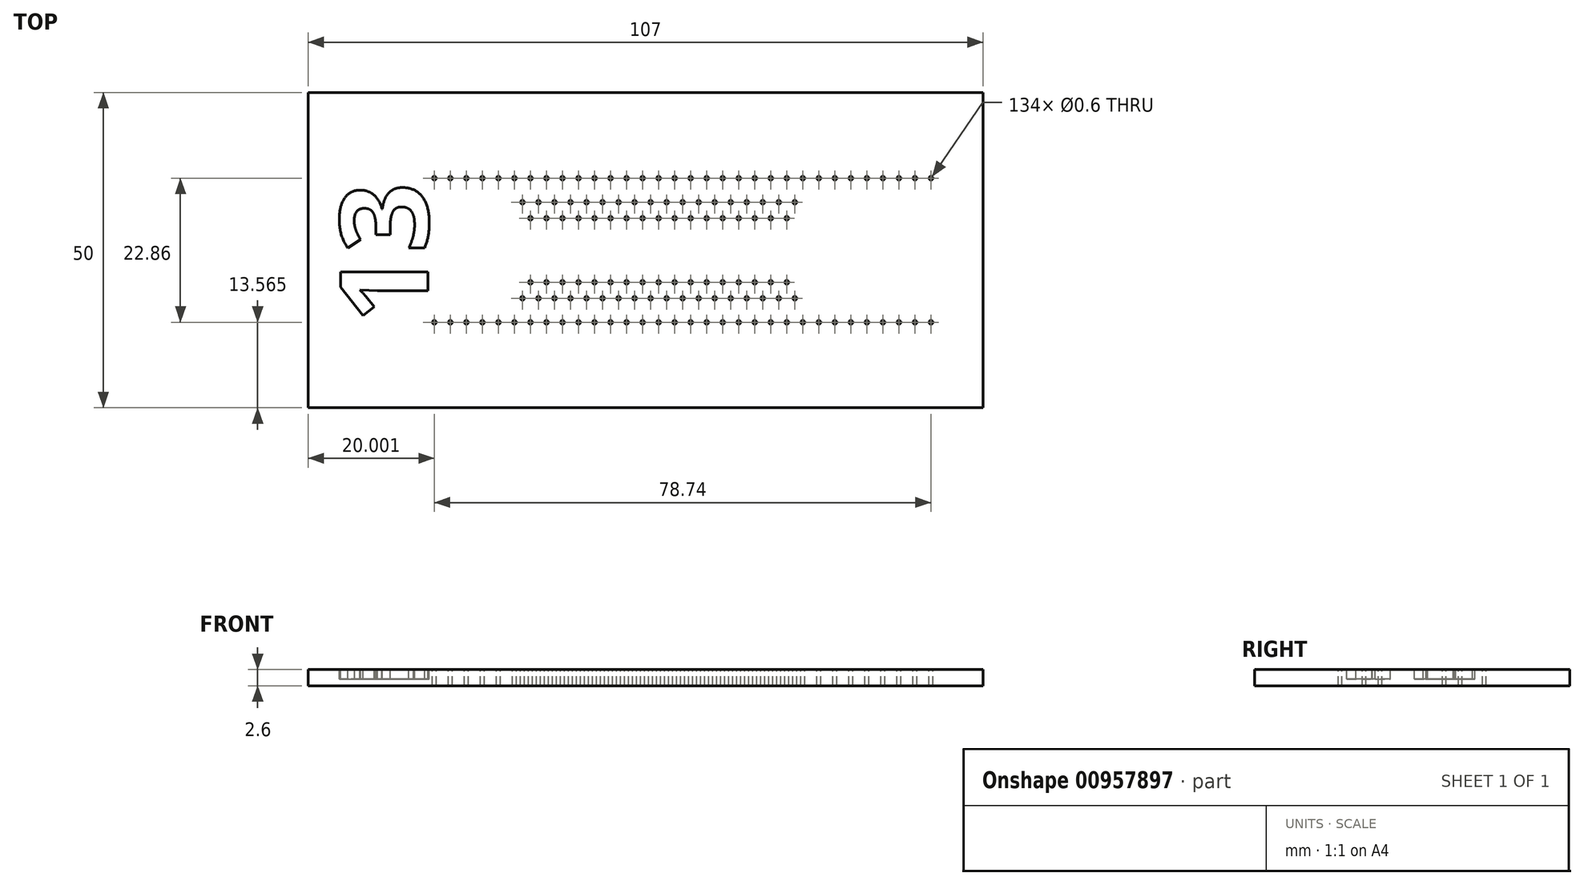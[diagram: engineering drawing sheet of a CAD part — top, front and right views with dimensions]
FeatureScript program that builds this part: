
annotation { "Feature Type Name" : "Feature", "Feature Type Description" : "" }
export const myFeature = defineFeature(function(context is Context, id is Id, definition is map)
    precondition{}
    {
        {
            var Q0;
            Q0=qCreatedBy(makeId("Top.planeOp"),FACE);
            var sketch = newSketch(context, id + "F0", { "sketchPlane" : qUnion([Q0])});
            skLineSegment(sketch, "E0.bottom", {"start": v(-43.16, 28.34) * mm, "end": v(63.84, 28.34) * mm});
            skLineSegment(sketch, "E0.top", {"start": v(-43.16, -21.66) * mm, "end": v(63.84, -21.66) * mm});
            skLineSegment(sketch, "E0.left", {"start": v(-43.16, 28.34) * mm, "end": v(-43.16, -21.66) * mm});
            skLineSegment(sketch, "E0.right", {"start": v(63.84, 28.34) * mm, "end": v(63.84, -21.66) * mm});
            skSolve(sketch);
        }
        {
            var Q0;
            Q0=makeQuery(id+"F0.imprint","IMPRINT",FACE,{"disambiguationData":[TD([[makeQuery(id+"F0.imprint","IMPRINT",EDGE,{"derivedFrom":sQuery(id+"F0.wireOp",EDGE,"E0.bottom")}),-1.0]])]});
            extrude(context, id + "F1", {"entities" : qUnion([Q0]), "depth" : 2.6 * mm, "offsetDistance" : 25 * mm});
        }
        {
            var Q0;
            Q0=makeQuery(id+"F1.opExtrude","CAP_FACE",FACE,{"disambiguationData":[OSD([sQuery(id+"F0.wireOp",EDGE,"E0.bottom"),sQuery(id+"F0.wireOp",EDGE,"E0.top"),sQuery(id+"F0.wireOp",EDGE,"E0.left"),sQuery(id+"F0.wireOp",EDGE,"E0.right")])],"isStart":false});
            var sketch = newSketch(context, id + "F2", { "sketchPlane" : qUnion([Q0])});
            skText(sketch, "E1", { "text": "13", "fontName": "OpenSans-Bold.ttf"});
            const initialGuessF2  = {"E1": [-0.02416, -0.00817, 0, 1, 0.014]};
            skSetInitialGuess(sketch, initialGuessF2);
            skSolve(sketch);
        }
        {
            var Q0;
            Q0=qSketchRegion(id+"F2",true);
            extrude(context, id + "F3", {"entities" : qUnion([Q0]), "operationType" : NewBodyOperationType.REMOVE, "oppositeDirection" : true, "depth" : 1.5 * mm, "offsetDistance" : 25 * mm});
        }
        {
            var Q0;
            {var subQ0=sQuery(id+"F0.wireOp",EDGE,"E0.left");var subQ1=sQuery(id+"F0.wireOp",EDGE,"E0.bottom");var subQ2=sQuery(id+"F0.wireOp",EDGE,"E0.right");var subQ3=sQuery(id+"F0.wireOp",EDGE,"E0.top");Q0=makeQuery(id+"F3.boolean.opBoolean","SPLIT",FACE,{"disambiguationData":[TD([makeQuery(id+"F1.opExtrude","SWEPT_FACE",FACE,{"disambiguationData":[OSD([subQ1])]})])],"derivedFrom":makeQuery(id+"F1.opExtrude","CAP_FACE",FACE,{"disambiguationData":[OSD([subQ1,subQ3,subQ0,subQ2])],"isStart":false})});}
            var sketch = newSketch(context, id + "F4", { "sketchPlane" : qUnion([Q0])});
            skCircle(sketch, "E2", {"center": v(-23.16, 14.77) * mm, "radius": 0.3 * mm});
            skCircle(sketch, "E3", {"center": v(-20.62, 14.77) * mm, "radius": 0.3 * mm});
            skCircle(sketch, "E4", {"center": v(-18.08, 14.77) * mm, "radius": 0.3 * mm});
            skCircle(sketch, "E5", {"center": v(-15.54, 14.77) * mm, "radius": 0.3 * mm});
            skCircle(sketch, "E6", {"center": v(-13, 14.77) * mm, "radius": 0.3 * mm});
            skCircle(sketch, "E7", {"center": v(-10.46, 14.77) * mm, "radius": 0.3 * mm});
            skCircle(sketch, "E8", {"center": v(-7.92, 14.77) * mm, "radius": 0.3 * mm});
            skCircle(sketch, "E9", {"center": v(-5.38, 14.77) * mm, "radius": 0.3 * mm});
            skCircle(sketch, "E10", {"center": v(-2.84, 14.77) * mm, "radius": 0.3 * mm});
            skCircle(sketch, "E11", {"center": v(-0.3, 14.77) * mm, "radius": 0.3 * mm});
            skCircle(sketch, "E12", {"center": v(2.24, 14.77) * mm, "radius": 0.3 * mm});
            skCircle(sketch, "E13", {"center": v(4.78, 14.77) * mm, "radius": 0.3 * mm});
            skCircle(sketch, "E14", {"center": v(7.32, 14.77) * mm, "radius": 0.3 * mm});
            skCircle(sketch, "E15", {"center": v(9.86, 14.77) * mm, "radius": 0.3 * mm});
            skCircle(sketch, "E16", {"center": v(12.4, 14.77) * mm, "radius": 0.3 * mm});
            skCircle(sketch, "E17", {"center": v(14.94, 14.77) * mm, "radius": 0.3 * mm});
            skCircle(sketch, "E18", {"center": v(17.48, 14.77) * mm, "radius": 0.3 * mm});
            skCircle(sketch, "E19", {"center": v(20.02, 14.77) * mm, "radius": 0.3 * mm});
            skCircle(sketch, "E20", {"center": v(22.56, 14.77) * mm, "radius": 0.3 * mm});
            skCircle(sketch, "E21", {"center": v(25.1, 14.77) * mm, "radius": 0.3 * mm});
            skCircle(sketch, "E22", {"center": v(27.64, 14.77) * mm, "radius": 0.3 * mm});
            skCircle(sketch, "E23", {"center": v(30.18, 14.77) * mm, "radius": 0.3 * mm});
            skCircle(sketch, "E24", {"center": v(32.72, 14.77) * mm, "radius": 0.3 * mm});
            skCircle(sketch, "E25", {"center": v(35.26, 14.77) * mm, "radius": 0.3 * mm});
            skCircle(sketch, "E26", {"center": v(37.8, 14.77) * mm, "radius": 0.3 * mm});
            skCircle(sketch, "E27", {"center": v(40.34, 14.77) * mm, "radius": 0.3 * mm});
            skCircle(sketch, "E28", {"center": v(42.88, 14.77) * mm, "radius": 0.3 * mm});
            skCircle(sketch, "E29", {"center": v(45.42, 14.77) * mm, "radius": 0.3 * mm});
            skCircle(sketch, "E30", {"center": v(47.96, 14.77) * mm, "radius": 0.3 * mm});
            skCircle(sketch, "E31", {"center": v(50.5, 14.77) * mm, "radius": 0.3 * mm});
            skCircle(sketch, "E32", {"center": v(53.04, 14.77) * mm, "radius": 0.3 * mm});
            skCircle(sketch, "E33", {"center": v(55.58, 14.77) * mm, "radius": 0.3 * mm});
            skCircle(sketch, "E34", {"center": v(-23.16, -8.1) * mm, "radius": 0.3 * mm});
            skCircle(sketch, "E35", {"center": v(-20.62, -8.1) * mm, "radius": 0.3 * mm});
            skCircle(sketch, "E36", {"center": v(-18.08, -8.1) * mm, "radius": 0.3 * mm});
            skCircle(sketch, "E37", {"center": v(-15.54, -8.1) * mm, "radius": 0.3 * mm});
            skCircle(sketch, "E38", {"center": v(-13, -8.1) * mm, "radius": 0.3 * mm});
            skCircle(sketch, "E39", {"center": v(-10.46, -8.1) * mm, "radius": 0.3 * mm});
            skCircle(sketch, "E40", {"center": v(-7.92, -8.1) * mm, "radius": 0.3 * mm});
            skCircle(sketch, "E41", {"center": v(-5.38, -8.1) * mm, "radius": 0.3 * mm});
            skCircle(sketch, "E42", {"center": v(-2.84, -8.1) * mm, "radius": 0.3 * mm});
            skCircle(sketch, "E43", {"center": v(-0.3, -8.1) * mm, "radius": 0.3 * mm});
            skCircle(sketch, "E44", {"center": v(2.24, -8.1) * mm, "radius": 0.3 * mm});
            skCircle(sketch, "E45", {"center": v(4.78, -8.1) * mm, "radius": 0.3 * mm});
            skCircle(sketch, "E46", {"center": v(7.32, -8.1) * mm, "radius": 0.3 * mm});
            skCircle(sketch, "E47", {"center": v(9.86, -8.1) * mm, "radius": 0.3 * mm});
            skCircle(sketch, "E48", {"center": v(12.4, -8.1) * mm, "radius": 0.3 * mm});
            skCircle(sketch, "E49", {"center": v(14.94, -8.1) * mm, "radius": 0.3 * mm});
            skCircle(sketch, "E50", {"center": v(17.48, -8.1) * mm, "radius": 0.3 * mm});
            skCircle(sketch, "E51", {"center": v(20.02, -8.1) * mm, "radius": 0.3 * mm});
            skCircle(sketch, "E52", {"center": v(22.56, -8.1) * mm, "radius": 0.3 * mm});
            skCircle(sketch, "E53", {"center": v(25.1, -8.1) * mm, "radius": 0.3 * mm});
            skCircle(sketch, "E54", {"center": v(27.64, -8.1) * mm, "radius": 0.3 * mm});
            skCircle(sketch, "E55", {"center": v(30.18, -8.1) * mm, "radius": 0.3 * mm});
            skCircle(sketch, "E56", {"center": v(32.72, -8.1) * mm, "radius": 0.3 * mm});
            skCircle(sketch, "E57", {"center": v(35.26, -8.1) * mm, "radius": 0.3 * mm});
            skCircle(sketch, "E58", {"center": v(37.8, -8.1) * mm, "radius": 0.3 * mm});
            skCircle(sketch, "E59", {"center": v(40.34, -8.1) * mm, "radius": 0.3 * mm});
            skCircle(sketch, "E60", {"center": v(42.88, -8.1) * mm, "radius": 0.3 * mm});
            skCircle(sketch, "E61", {"center": v(45.42, -8.1) * mm, "radius": 0.3 * mm});
            skCircle(sketch, "E62", {"center": v(47.96, -8.1) * mm, "radius": 0.3 * mm});
            skCircle(sketch, "E63", {"center": v(50.5, -8.1) * mm, "radius": 0.3 * mm});
            skCircle(sketch, "E64", {"center": v(53.04, -8.1) * mm, "radius": 0.3 * mm});
            skCircle(sketch, "E65", {"center": v(55.58, -8.1) * mm, "radius": 0.3 * mm});
            skCircle(sketch, "E66", {"center": v(-9.19, 10.96) * mm, "radius": 0.3 * mm});
            skCircle(sketch, "E67", {"center": v(-6.65, 10.96) * mm, "radius": 0.3 * mm});
            skCircle(sketch, "E68", {"center": v(-4.1, 10.96) * mm, "radius": 0.3 * mm});
            skCircle(sketch, "E69", {"center": v(-1.57, 10.96) * mm, "radius": 0.3 * mm});
            skCircle(sketch, "E70", {"center": v(0.97, 10.96) * mm, "radius": 0.3 * mm});
            skCircle(sketch, "E71", {"center": v(3.51, 10.96) * mm, "radius": 0.3 * mm});
            skCircle(sketch, "E72", {"center": v(6.05, 10.96) * mm, "radius": 0.3 * mm});
            skCircle(sketch, "E73", {"center": v(8.6, 10.96) * mm, "radius": 0.3 * mm});
            skCircle(sketch, "E74", {"center": v(11.13, 10.96) * mm, "radius": 0.3 * mm});
            skCircle(sketch, "E75", {"center": v(13.67, 10.96) * mm, "radius": 0.3 * mm});
            skCircle(sketch, "E76", {"center": v(16.21, 10.96) * mm, "radius": 0.3 * mm});
            skCircle(sketch, "E77", {"center": v(18.75, 10.96) * mm, "radius": 0.3 * mm});
            skCircle(sketch, "E78", {"center": v(21.3, 10.96) * mm, "radius": 0.3 * mm});
            skCircle(sketch, "E79", {"center": v(23.83, 10.96) * mm, "radius": 0.3 * mm});
            skCircle(sketch, "E80", {"center": v(26.37, 10.96) * mm, "radius": 0.3 * mm});
            skCircle(sketch, "E81", {"center": v(28.91, 10.96) * mm, "radius": 0.3 * mm});
            skCircle(sketch, "E82", {"center": v(31.45, 10.96) * mm, "radius": 0.3 * mm});
            skCircle(sketch, "E83", {"center": v(34, 10.96) * mm, "radius": 0.3 * mm});
            skCircle(sketch, "E84", {"center": v(-7.92, 8.42) * mm, "radius": 0.3 * mm});
            skCircle(sketch, "E85", {"center": v(-5.38, 8.42) * mm, "radius": 0.3 * mm});
            skCircle(sketch, "E86", {"center": v(-2.84, 8.42) * mm, "radius": 0.3 * mm});
            skCircle(sketch, "E87", {"center": v(-0.3, 8.42) * mm, "radius": 0.3 * mm});
            skCircle(sketch, "E88", {"center": v(2.24, 8.42) * mm, "radius": 0.3 * mm});
            skCircle(sketch, "E89", {"center": v(4.78, 8.42) * mm, "radius": 0.3 * mm});
            skCircle(sketch, "E90", {"center": v(7.32, 8.42) * mm, "radius": 0.3 * mm});
            skCircle(sketch, "E91", {"center": v(9.86, 8.42) * mm, "radius": 0.3 * mm});
            skCircle(sketch, "E92", {"center": v(12.4, 8.42) * mm, "radius": 0.3 * mm});
            skCircle(sketch, "E93", {"center": v(14.94, 8.42) * mm, "radius": 0.3 * mm});
            skCircle(sketch, "E94", {"center": v(17.48, 8.42) * mm, "radius": 0.3 * mm});
            skCircle(sketch, "E95", {"center": v(20.02, 8.42) * mm, "radius": 0.3 * mm});
            skCircle(sketch, "E96", {"center": v(22.56, 8.42) * mm, "radius": 0.3 * mm});
            skCircle(sketch, "E97", {"center": v(25.1, 8.42) * mm, "radius": 0.3 * mm});
            skCircle(sketch, "E98", {"center": v(27.64, 8.42) * mm, "radius": 0.3 * mm});
            skCircle(sketch, "E99", {"center": v(30.18, 8.42) * mm, "radius": 0.3 * mm});
            skCircle(sketch, "E100", {"center": v(32.72, 8.42) * mm, "radius": 0.3 * mm});
            skCircle(sketch, "E101", {"center": v(-9.19, -4.28) * mm, "radius": 0.3 * mm});
            skCircle(sketch, "E102", {"center": v(-6.65, -4.28) * mm, "radius": 0.3 * mm});
            skCircle(sketch, "E103", {"center": v(-4.1, -4.28) * mm, "radius": 0.3 * mm});
            skCircle(sketch, "E104", {"center": v(-1.57, -4.28) * mm, "radius": 0.3 * mm});
            skCircle(sketch, "E105", {"center": v(0.97, -4.28) * mm, "radius": 0.3 * mm});
            skCircle(sketch, "E106", {"center": v(3.51, -4.28) * mm, "radius": 0.3 * mm});
            skCircle(sketch, "E107", {"center": v(6.05, -4.28) * mm, "radius": 0.3 * mm});
            skCircle(sketch, "E108", {"center": v(8.6, -4.28) * mm, "radius": 0.3 * mm});
            skCircle(sketch, "E109", {"center": v(11.13, -4.28) * mm, "radius": 0.3 * mm});
            skCircle(sketch, "E110", {"center": v(13.67, -4.28) * mm, "radius": 0.3 * mm});
            skCircle(sketch, "E111", {"center": v(16.21, -4.28) * mm, "radius": 0.3 * mm});
            skCircle(sketch, "E112", {"center": v(18.75, -4.28) * mm, "radius": 0.3 * mm});
            skCircle(sketch, "E113", {"center": v(21.3, -4.28) * mm, "radius": 0.3 * mm});
            skCircle(sketch, "E114", {"center": v(23.83, -4.28) * mm, "radius": 0.3 * mm});
            skCircle(sketch, "E115", {"center": v(26.37, -4.28) * mm, "radius": 0.3 * mm});
            skCircle(sketch, "E116", {"center": v(28.91, -4.28) * mm, "radius": 0.3 * mm});
            skCircle(sketch, "E117", {"center": v(31.45, -4.28) * mm, "radius": 0.3 * mm});
            skCircle(sketch, "E118", {"center": v(34, -4.28) * mm, "radius": 0.3 * mm});
            skCircle(sketch, "E119", {"center": v(-7.92, -1.74) * mm, "radius": 0.3 * mm});
            skCircle(sketch, "E120", {"center": v(-5.38, -1.74) * mm, "radius": 0.3 * mm});
            skCircle(sketch, "E121", {"center": v(-2.84, -1.74) * mm, "radius": 0.3 * mm});
            skCircle(sketch, "E122", {"center": v(-0.3, -1.74) * mm, "radius": 0.3 * mm});
            skCircle(sketch, "E123", {"center": v(2.24, -1.74) * mm, "radius": 0.3 * mm});
            skCircle(sketch, "E124", {"center": v(4.78, -1.74) * mm, "radius": 0.3 * mm});
            skCircle(sketch, "E125", {"center": v(7.32, -1.74) * mm, "radius": 0.3 * mm});
            skCircle(sketch, "E126", {"center": v(9.86, -1.74) * mm, "radius": 0.3 * mm});
            skCircle(sketch, "E127", {"center": v(12.4, -1.74) * mm, "radius": 0.3 * mm});
            skCircle(sketch, "E128", {"center": v(14.94, -1.74) * mm, "radius": 0.3 * mm});
            skCircle(sketch, "E129", {"center": v(17.48, -1.74) * mm, "radius": 0.3 * mm});
            skCircle(sketch, "E130", {"center": v(20.02, -1.74) * mm, "radius": 0.3 * mm});
            skCircle(sketch, "E131", {"center": v(22.56, -1.74) * mm, "radius": 0.3 * mm});
            skCircle(sketch, "E132", {"center": v(25.1, -1.74) * mm, "radius": 0.3 * mm});
            skCircle(sketch, "E133", {"center": v(27.64, -1.74) * mm, "radius": 0.3 * mm});
            skCircle(sketch, "E134", {"center": v(30.18, -1.74) * mm, "radius": 0.3 * mm});
            skCircle(sketch, "E135", {"center": v(32.72, -1.74) * mm, "radius": 0.3 * mm});
            skSolve(sketch);
        }
        {
            var Q0;
            Q0 = qSketchRegion(id + "F4", true);
            extrude(context, id + "F5", {"entities" : qUnion([Q0]), "operationType" : NewBodyOperationType.REMOVE, "endBound" : BoundingType.UP_TO_NEXT, "oppositeDirection" : true, "depth" : 25 * mm, "offsetDistance" : 25 * mm});
        }
    });
